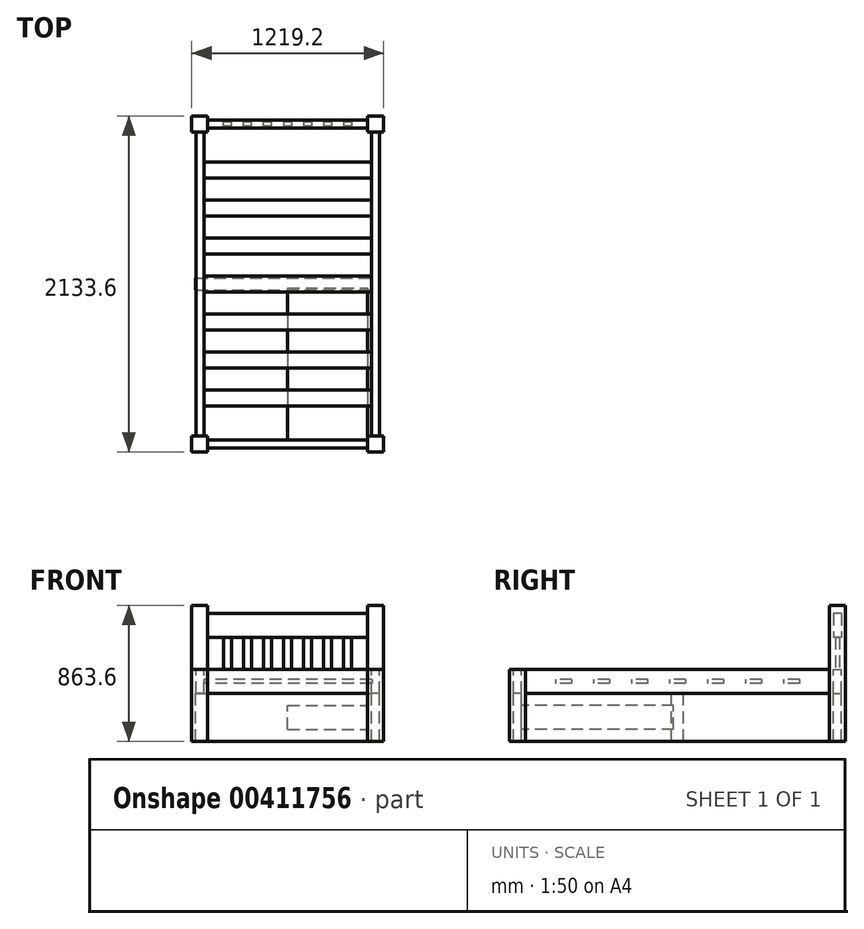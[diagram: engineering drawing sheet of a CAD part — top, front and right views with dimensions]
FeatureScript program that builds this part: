
annotation { "Feature Type Name" : "Feature", "Feature Type Description" : "" }
export const myFeature = defineFeature(function(context is Context, id is Id, definition is map)
    precondition{}
    {
        {
            var Q0;
            Q0=qCreatedBy(makeId("Top.planeOp"),FACE);
            var sketch = newSketch(context, id + "F0", { "sketchPlane" : qUnion([Q0])});
            skLineSegment(sketch, "E0.bottom", {"start": v(0, 0) * mm, "end": v(1219.2, 0) * mm});
            skLineSegment(sketch, "E0.top", {"start": v(0, 2133.6) * mm, "end": v(1219.2, 2133.6) * mm});
            skLineSegment(sketch, "E0.left", {"start": v(0, 0) * mm, "end": v(0, 2133.6) * mm});
            skLineSegment(sketch, "E0.right", {"start": v(1219.2, 0) * mm, "end": v(1219.2, 2133.6) * mm});
            skSolve(sketch);
        }
        {
            var Q0;
            Q0 = qSketchRegion(id + "F0", true);
            extrude(context, id + "F1", {"entities" : qUnion([Q0]), "depth" : 609.6 * mm});
        }
        {
            var Q0;
            Q0=makeQuery(id+"F1.opExtrude","CAP_FACE",FACE,{"disambiguationData":[OSD([sQuery(id+"F0.wireOp",EDGE,"E0.bottom"),sQuery(id+"F0.wireOp",EDGE,"E0.top"),sQuery(id+"F0.wireOp",EDGE,"E0.left"),sQuery(id+"F0.wireOp",EDGE,"E0.right")])],"isStart":false});
            var sketch = newSketch(context, id + "F2", { "sketchPlane" : qUnion([Q0])});
            skLineSegment(sketch, "E1.bottom", {"start": v(101.6, 0) * mm, "end": v(0, 0) * mm});
            skLineSegment(sketch, "E1.top", {"start": v(101.6, 101.6) * mm, "end": v(0, 101.6) * mm});
            skLineSegment(sketch, "E1.left", {"start": v(101.6, 0) * mm, "end": v(101.6, 101.6) * mm});
            skLineSegment(sketch, "E1.right", {"start": v(0, 0) * mm, "end": v(0, 101.6) * mm});
            skLineSegment(sketch, "E2.bottom", {"start": v(1117.6, 0) * mm, "end": v(1219.2, 0) * mm});
            skLineSegment(sketch, "E2.top", {"start": v(1117.6, 101.6) * mm, "end": v(1219.2, 101.6) * mm});
            skLineSegment(sketch, "E2.left", {"start": v(1117.6, 0) * mm, "end": v(1117.6, 101.6) * mm});
            skLineSegment(sketch, "E2.right", {"start": v(1219.2, 0) * mm, "end": v(1219.2, 101.6) * mm});
            skLineSegment(sketch, "E3.bottom", {"start": v(0, 2133.6) * mm, "end": v(101.6, 2133.6) * mm});
            skLineSegment(sketch, "E3.top", {"start": v(0, 2032) * mm, "end": v(101.6, 2032) * mm});
            skLineSegment(sketch, "E3.left", {"start": v(0, 2133.6) * mm, "end": v(0, 2032) * mm});
            skLineSegment(sketch, "E3.right", {"start": v(101.6, 2133.6) * mm, "end": v(101.6, 2032) * mm});
            skLineSegment(sketch, "E4.bottom", {"start": v(1219.2, 2133.6) * mm, "end": v(1117.6, 2133.6) * mm});
            skLineSegment(sketch, "E4.top", {"start": v(1219.2, 2032) * mm, "end": v(1117.6, 2032) * mm});
            skLineSegment(sketch, "E4.left", {"start": v(1219.2, 2133.6) * mm, "end": v(1219.2, 2032) * mm});
            skLineSegment(sketch, "E4.right", {"start": v(1117.6, 2133.6) * mm, "end": v(1117.6, 2032) * mm});
            skSolve(sketch);
        }
        {
            var Q0;
            {var subQ3=sQuery(id+"F2.wireOp",EDGE,"E1.top");Q0=makeQuery(id+"F2.imprint","IMPRINT",FACE,{"disambiguationData":[TD([[makeQuery(id+"F2.imprint","IMPRINT",EDGE,{"derivedFrom":subQ3}),-1.0]])]});}
            extrude(context, id + "F3", {"entities" : qUnion([Q0]), "operationType" : NewBodyOperationType.REMOVE, "oppositeDirection" : true, "depth" : 609.6 * mm});
        }
        {
            var Q0;
            Q0=makeQuery(id+"F3.boolean.opBoolean","COPY",FACE,{"derivedFrom":makeQuery(id+"F3.opExtrude","SWEPT_FACE",FACE,{"disambiguationData":[OSD([sQuery(id+"F2.wireOp",EDGE,"E3.top")])]})});
            var sketch = newSketch(context, id + "F4", { "sketchPlane" : qUnion([Q0])});
            skLineSegment(sketch, "E5", {"start": v(50.8, 0) * mm, "end": v(50.8, 609.6) * mm});
            skLineSegment(sketch, "E6", {"start": v(50.8, 0) * mm, "end": v(50.8, 304.8) * mm});
            skLineSegment(sketch, "E7.bottom", {"start": v(50.8, 304.8) * mm, "end": v(27.17, 304.8) * mm});
            skLineSegment(sketch, "E7.top", {"start": v(50.8, 457.2) * mm, "end": v(27.17, 457.2) * mm});
            skLineSegment(sketch, "E7.left", {"start": v(50.8, 304.8) * mm, "end": v(50.8, 457.2) * mm});
            skLineSegment(sketch, "E7.right", {"start": v(27.17, 304.8) * mm, "end": v(27.17, 457.2) * mm});
            skLineSegment(sketch, "E8.bottom", {"start": v(50.8, 304.8) * mm, "end": v(77.97, 304.8) * mm});
            skLineSegment(sketch, "E8.top", {"start": v(50.8, 457.2) * mm, "end": v(77.97, 457.2) * mm});
            skLineSegment(sketch, "E8.right", {"start": v(77.97, 304.8) * mm, "end": v(77.97, 457.2) * mm});
            skSolve(sketch);
        }
        {
            var Q0;
            Q0 = qSketchRegion(id + "F4", true);
            extrude(context, id + "F5", {"entities" : qUnion([Q0]), "depth" : 1930.4 * mm});
        }
        {
            var Q0;
            Q0=makeQuery(id+"F3.boolean.opBoolean","COPY",FACE,{"derivedFrom":makeQuery(id+"F3.opExtrude","SWEPT_FACE",FACE,{"disambiguationData":[OSD([sQuery(id+"F2.wireOp",EDGE,"E1.left")])]})});
            var sketch = newSketch(context, id + "F6", { "sketchPlane" : qUnion([Q0])});
            skLineSegment(sketch, "E9", {"start": v(50.8, 0) * mm, "end": v(50.8, 609.6) * mm});
            skLineSegment(sketch, "E10", {"start": v(50.8, 609.6) * mm, "end": v(50.8, 304.8) * mm});
            skLineSegment(sketch, "E11.bottom", {"start": v(50.8, 304.8) * mm, "end": v(25.4, 304.8) * mm});
            skLineSegment(sketch, "E11.top", {"start": v(50.8, 457.2) * mm, "end": v(25.4, 457.2) * mm});
            skLineSegment(sketch, "E11.left", {"start": v(50.8, 304.8) * mm, "end": v(50.8, 457.2) * mm});
            skLineSegment(sketch, "E11.right", {"start": v(25.4, 304.8) * mm, "end": v(25.4, 457.2) * mm});
            skLineSegment(sketch, "E12.bottom", {"start": v(50.8, 304.8) * mm, "end": v(76.2, 304.8) * mm});
            skLineSegment(sketch, "E12.top", {"start": v(50.8, 457.2) * mm, "end": v(76.2, 457.2) * mm});
            skLineSegment(sketch, "E12.right", {"start": v(76.2, 304.8) * mm, "end": v(76.2, 457.2) * mm});
            skSolve(sketch);
        }
        {
            var Q0;
            Q0=makeQuery(id+"F6.imprint","IMPRINT",FACE,{"disambiguationData":[TD([[makeQuery(id+"F6.imprint","IMPRINT",EDGE,{"derivedFrom":sQuery(id+"F6.wireOp",EDGE,"E11.bottom")}),-1.0]])]});
            var Q1;
            Q1=makeQuery(id+"F6.imprint","IMPRINT",FACE,{"disambiguationData":[TD([[makeQuery(id+"F6.imprint","IMPRINT",EDGE,{"derivedFrom":sQuery(id+"F6.wireOp",EDGE,"E12.bottom")}),1.0]])]});
            extrude(context, id + "F7", {"entities" : qUnion([Q0, Q1]), "depth" : 1016 * mm});
        }
        {
            var Q0;
            Q0=makeQuery(id+"F3.boolean.opBoolean","COPY",FACE,{"derivedFrom":makeQuery(id+"F3.opExtrude","SWEPT_FACE",FACE,{"disambiguationData":[OSD([sQuery(id+"F2.wireOp",EDGE,"E2.top")])]})});
            var sketch = newSketch(context, id + "F8", { "sketchPlane" : qUnion([Q0])});
            skLineSegment(sketch, "E13", {"start": v(-1168.4, 0) * mm, "end": v(-1168.4, 609.6) * mm});
            skLineSegment(sketch, "E14", {"start": v(-1168.4, 609.6) * mm, "end": v(-1168.4, 304.8) * mm});
            skLineSegment(sketch, "E15.bottom", {"start": v(-1168.4, 304.8) * mm, "end": v(-1193.8, 304.8) * mm});
            skLineSegment(sketch, "E15.top", {"start": v(-1168.4, 457.2) * mm, "end": v(-1193.8, 457.2) * mm});
            skLineSegment(sketch, "E15.left", {"start": v(-1168.4, 304.8) * mm, "end": v(-1168.4, 457.2) * mm});
            skLineSegment(sketch, "E15.right", {"start": v(-1193.8, 304.8) * mm, "end": v(-1193.8, 457.2) * mm});
            skLineSegment(sketch, "E16.bottom", {"start": v(-1168.4, 304.8) * mm, "end": v(-1143, 304.8) * mm});
            skLineSegment(sketch, "E16.top", {"start": v(-1168.4, 457.2) * mm, "end": v(-1143, 457.2) * mm});
            skLineSegment(sketch, "E16.right", {"start": v(-1143, 304.8) * mm, "end": v(-1143, 457.2) * mm});
            skSolve(sketch);
        }
        {
            var Q0;
            Q0=makeQuery(id+"F8.imprint","IMPRINT",FACE,{"disambiguationData":[TD([[makeQuery(id+"F8.imprint","IMPRINT",EDGE,{"derivedFrom":sQuery(id+"F8.wireOp",EDGE,"E16.bottom")}),1.0]])]});
            var Q1;
            Q1=makeQuery(id+"F8.imprint","IMPRINT",FACE,{"disambiguationData":[TD([[makeQuery(id+"F8.imprint","IMPRINT",EDGE,{"derivedFrom":sQuery(id+"F8.wireOp",EDGE,"E16.bottom")}),1.0]])]});
            var Q2;
            Q2=makeQuery(id+"F8.imprint","IMPRINT",FACE,{"disambiguationData":[TD([[makeQuery(id+"F8.imprint","IMPRINT",EDGE,{"derivedFrom":sQuery(id+"F8.wireOp",EDGE,"E15.bottom")}),-1.0]])]});
            extrude(context, id + "F9", {"entities" : qUnion([Q0, Q1, Q2]), "depth" : 1930.4 * mm});
        }
        {
            var Q0;
            Q0=makeQuery(id+"F3.boolean.opBoolean","COPY",FACE,{"derivedFrom":makeQuery(id+"F3.opExtrude","SWEPT_FACE",FACE,{"disambiguationData":[OSD([sQuery(id+"F2.wireOp",EDGE,"E4.right")])]})});
            var sketch = newSketch(context, id + "F10", { "sketchPlane" : qUnion([Q0])});
            skLineSegment(sketch, "E17", {"start": v(-2082.8, 0) * mm, "end": v(-2082.8, 609.6) * mm});
            skLineSegment(sketch, "E18", {"start": v(-2082.8, 0) * mm, "end": v(-2082.8, 304.8) * mm});
            skLineSegment(sketch, "E19.bottom", {"start": v(-2082.8, 304.8) * mm, "end": v(-2108.2, 304.8) * mm});
            skLineSegment(sketch, "E19.top", {"start": v(-2082.8, 457.2) * mm, "end": v(-2108.2, 457.2) * mm});
            skLineSegment(sketch, "E19.left", {"start": v(-2082.8, 304.8) * mm, "end": v(-2082.8, 457.2) * mm});
            skLineSegment(sketch, "E19.right", {"start": v(-2108.2, 304.8) * mm, "end": v(-2108.2, 457.2) * mm});
            skLineSegment(sketch, "E20.bottom", {"start": v(-2082.8, 304.8) * mm, "end": v(-2057.4, 304.8) * mm});
            skLineSegment(sketch, "E20.top", {"start": v(-2082.8, 457.2) * mm, "end": v(-2057.4, 457.2) * mm});
            skLineSegment(sketch, "E20.right", {"start": v(-2057.4, 304.8) * mm, "end": v(-2057.4, 457.2) * mm});
            skSolve(sketch);
        }
        {
            var Q0;
            Q0 = qSketchRegion(id + "F10", true);
            extrude(context, id + "F11", {"entities" : qUnion([Q0]), "depth" : 1016 * mm});
        }
        {
            var Q0;
            {var subQ0=sQuery(id+"F0.wireOp",EDGE,"E0.bottom");var subQ1=sQuery(id+"F0.wireOp",EDGE,"E0.left");Q0=makeQuery(id+"F3.boolean.opBoolean","SPLIT",FACE,{"disambiguationData":[TD([makeQuery(id+"F3.opExtrude","SWEPT_FACE",FACE,{"disambiguationData":[OSD([sQuery(id+"F2.wireOp",EDGE,"E1.top")])]})])],"derivedFrom":makeQuery(id+"F1.opExtrude","CAP_FACE",FACE,{"disambiguationData":[OSD([subQ0,sQuery(id+"F0.wireOp",EDGE,"E0.top"),subQ1,sQuery(id+"F0.wireOp",EDGE,"E0.right")])],"isStart":false})});}
            var sketch = newSketch(context, id + "F12", { "sketchPlane" : qUnion([Q0])});
            skSolve(sketch);
        }
        {
            var Q0;
            Q0=makeQuery(id+"F5.opExtrude","SWEPT_FACE",FACE,{"disambiguationData":[OSD([sQuery(id+"F4.wireOp",EDGE,"E8.right")])]});
            var sketch = newSketch(context, id + "F13", { "sketchPlane" : qUnion([Q0])});
            skLineSegment(sketch, "E21", {"start": v(101.6, 381) * mm, "end": v(342.9, 381) * mm});
            skPoint(sketch, "E21.endSnap0", {"position": v(101.6, 381) * mm});
            skLineSegment(sketch, "E22", {"start": v(1066.8, 381) * mm, "end": v(342.9, 381) * mm});
            skLineSegment(sketch, "E23", {"start": v(1790.7, 381) * mm, "end": v(1066.8, 381) * mm});
            skLineSegment(sketch, "E24", {"start": v(2032, 381) * mm, "end": v(1790.7, 381) * mm});
            skLineSegment(sketch, "E25", {"start": v(342.9, 381) * mm, "end": v(584.2, 381) * mm});
            skLineSegment(sketch, "E26", {"start": v(825.5, 381) * mm, "end": v(584.2, 381) * mm});
            skLineSegment(sketch, "E27", {"start": v(1549.4, 381) * mm, "end": v(1790.7, 381) * mm});
            skLineSegment(sketch, "E28", {"start": v(1308.1, 381) * mm, "end": v(1549.4, 381) * mm});
            skLineSegment(sketch, "E29.bottom", {"start": v(393.7, 393.7) * mm, "end": v(292.1, 393.7) * mm});
            skLineSegment(sketch, "E29.top", {"start": v(393.7, 368.3) * mm, "end": v(292.1, 368.3) * mm});
            skLineSegment(sketch, "E29.left", {"start": v(393.7, 393.7) * mm, "end": v(393.7, 368.3) * mm});
            skLineSegment(sketch, "E29.right", {"start": v(292.1, 393.7) * mm, "end": v(292.1, 368.3) * mm});
            skPoint(sketch, "E29.middle", {"position": v(342.9, 381) * mm});
            skLineSegment(sketch, "E30.bottom", {"start": v(292.1, 393.7) * mm, "end": v(393.7, 393.7) * mm});
            skLineSegment(sketch, "E30.top", {"start": v(292.1, 393.7) * mm, "end": v(393.7, 393.7) * mm});
            skLineSegment(sketch, "E30.left", {"start": v(292.1, 393.7) * mm, "end": v(292.1, 393.7) * mm});
            skLineSegment(sketch, "E30.right", {"start": v(393.7, 393.7) * mm, "end": v(393.7, 393.7) * mm});
            skPoint(sketch, "E30.middle", {"position": v(342.9, 393.7) * mm});
            skLineSegment(sketch, "E31.bottom", {"start": v(635, 393.7) * mm, "end": v(533.4, 393.7) * mm});
            skLineSegment(sketch, "E31.top", {"start": v(635, 368.3) * mm, "end": v(533.4, 368.3) * mm});
            skLineSegment(sketch, "E31.left", {"start": v(635, 393.7) * mm, "end": v(635, 368.3) * mm});
            skLineSegment(sketch, "E31.right", {"start": v(533.4, 393.7) * mm, "end": v(533.4, 368.3) * mm});
            skPoint(sketch, "E31.middle", {"position": v(584.2, 381) * mm});
            skLineSegment(sketch, "E32.bottom", {"start": v(876.3, 393.7) * mm, "end": v(774.7, 393.7) * mm});
            skLineSegment(sketch, "E32.top", {"start": v(876.3, 368.3) * mm, "end": v(774.7, 368.3) * mm});
            skLineSegment(sketch, "E32.left", {"start": v(876.3, 393.7) * mm, "end": v(876.3, 368.3) * mm});
            skLineSegment(sketch, "E32.right", {"start": v(774.7, 393.7) * mm, "end": v(774.7, 368.3) * mm});
            skPoint(sketch, "E32.middle", {"position": v(825.5, 381) * mm});
            skLineSegment(sketch, "E33.bottom", {"start": v(1117.6, 393.7) * mm, "end": v(1016, 393.7) * mm});
            skLineSegment(sketch, "E33.top", {"start": v(1117.6, 368.3) * mm, "end": v(1016, 368.3) * mm});
            skLineSegment(sketch, "E33.left", {"start": v(1117.6, 393.7) * mm, "end": v(1117.6, 368.3) * mm});
            skLineSegment(sketch, "E33.right", {"start": v(1016, 393.7) * mm, "end": v(1016, 368.3) * mm});
            skPoint(sketch, "E33.middle", {"position": v(1066.8, 381) * mm});
            skLineSegment(sketch, "E34.bottom", {"start": v(1358.9, 393.7) * mm, "end": v(1257.3, 393.7) * mm});
            skLineSegment(sketch, "E34.top", {"start": v(1358.9, 368.3) * mm, "end": v(1257.3, 368.3) * mm});
            skLineSegment(sketch, "E34.left", {"start": v(1358.9, 393.7) * mm, "end": v(1358.9, 368.3) * mm});
            skLineSegment(sketch, "E34.right", {"start": v(1257.3, 393.7) * mm, "end": v(1257.3, 368.3) * mm});
            skPoint(sketch, "E34.middle", {"position": v(1308.1, 381) * mm});
            skLineSegment(sketch, "E35.bottom", {"start": v(1600.2, 393.7) * mm, "end": v(1498.6, 393.7) * mm});
            skLineSegment(sketch, "E35.top", {"start": v(1600.2, 368.3) * mm, "end": v(1498.6, 368.3) * mm});
            skLineSegment(sketch, "E35.left", {"start": v(1600.2, 393.7) * mm, "end": v(1600.2, 368.3) * mm});
            skLineSegment(sketch, "E35.right", {"start": v(1498.6, 393.7) * mm, "end": v(1498.6, 368.3) * mm});
            skPoint(sketch, "E35.middle", {"position": v(1549.4, 381) * mm});
            skLineSegment(sketch, "E36.bottom", {"start": v(1841.5, 393.7) * mm, "end": v(1739.9, 393.7) * mm});
            skLineSegment(sketch, "E36.top", {"start": v(1841.5, 368.3) * mm, "end": v(1739.9, 368.3) * mm});
            skLineSegment(sketch, "E36.left", {"start": v(1841.5, 393.7) * mm, "end": v(1841.5, 368.3) * mm});
            skLineSegment(sketch, "E36.right", {"start": v(1739.9, 393.7) * mm, "end": v(1739.9, 368.3) * mm});
            skPoint(sketch, "E36.middle", {"position": v(1790.7, 381) * mm});
            skSolve(sketch);
        }
        {
            var Q0;
            Q0 = qSketchRegion(id + "F13", true);
            extrude(context, id + "F14", {"entities" : qUnion([Q0]), "depth" : 1066.8 * mm});
        }
        {
            var Q0;
            {var subQ0=sQuery(id+"F0.wireOp",EDGE,"E0.top");var subQ1=sQuery(id+"F0.wireOp",EDGE,"E0.right");Q0=makeQuery(id+"F3.boolean.opBoolean","SPLIT",FACE,{"disambiguationData":[TD([makeQuery(id+"F3.opExtrude","SWEPT_FACE",FACE,{"disambiguationData":[OSD([sQuery(id+"F2.wireOp",EDGE,"E4.top")])]})])],"derivedFrom":makeQuery(id+"F1.opExtrude","CAP_FACE",FACE,{"disambiguationData":[OSD([sQuery(id+"F0.wireOp",EDGE,"E0.bottom"),subQ0,sQuery(id+"F0.wireOp",EDGE,"E0.left"),subQ1])],"isStart":false})});}
            var sketch = newSketch(context, id + "F15", { "sketchPlane" : qUnion([Q0])});
            skLineSegment(sketch, "E37.bottom", {"start": v(1117.6, 2032) * mm, "end": v(1219.2, 2032) * mm});
            skLineSegment(sketch, "E37.top", {"start": v(1117.6, 2133.6) * mm, "end": v(1219.2, 2133.6) * mm});
            skLineSegment(sketch, "E37.left", {"start": v(1117.6, 2032) * mm, "end": v(1117.6, 2133.6) * mm});
            skLineSegment(sketch, "E37.right", {"start": v(1219.2, 2032) * mm, "end": v(1219.2, 2133.6) * mm});
            skSolve(sketch);
        }
        {
            var Q0;
            Q0 = qSketchRegion(id + "F15", true);
            extrude(context, id + "F16", {"entities" : qUnion([Q0]), "operationType" : NewBodyOperationType.ADD, "depth" : 254 * mm});
        }
        {
            var Q0;
            {var subQ0=sQuery(id+"F0.wireOp",EDGE,"E0.top");var subQ1=sQuery(id+"F0.wireOp",EDGE,"E0.left");Q0=makeQuery(id+"F3.boolean.opBoolean","SPLIT",FACE,{"disambiguationData":[TD([makeQuery(id+"F3.opExtrude","SWEPT_FACE",FACE,{"disambiguationData":[OSD([sQuery(id+"F2.wireOp",EDGE,"E3.top")])]})])],"derivedFrom":makeQuery(id+"F1.opExtrude","CAP_FACE",FACE,{"disambiguationData":[OSD([sQuery(id+"F0.wireOp",EDGE,"E0.bottom"),subQ0,subQ1,sQuery(id+"F0.wireOp",EDGE,"E0.right")])],"isStart":false})});}
            var sketch = newSketch(context, id + "F17", { "sketchPlane" : qUnion([Q0])});
            skLineSegment(sketch, "E38.bottom", {"start": v(0, 2032) * mm, "end": v(101.6, 2032) * mm});
            skLineSegment(sketch, "E38.top", {"start": v(0, 2133.6) * mm, "end": v(101.6, 2133.6) * mm});
            skLineSegment(sketch, "E38.left", {"start": v(0, 2032) * mm, "end": v(0, 2133.6) * mm});
            skLineSegment(sketch, "E38.right", {"start": v(101.6, 2032) * mm, "end": v(101.6, 2133.6) * mm});
            skSolve(sketch);
        }
        {
            var Q0;
            Q0 = qSketchRegion(id + "F17", true);
            extrude(context, id + "F18", {"entities" : qUnion([Q0]), "operationType" : NewBodyOperationType.ADD, "depth" : 254 * mm});
        }
        {
            var Q0;
            Q0=makeQuery(id+"F18.boolean.opBoolean","MERGE",FACE,{"derivedFrom":[makeQuery(id+"F3.boolean.opBoolean","COPY",FACE,{"derivedFrom":makeQuery(id+"F3.opExtrude","SWEPT_FACE",FACE,{"disambiguationData":[OSD([sQuery(id+"F2.wireOp",EDGE,"E3.right")])]})}),makeQuery(id+"F18.opExtrude","SWEPT_FACE",FACE,{"disambiguationData":[OSD([sQuery(id+"F17.wireOp",EDGE,"E38.right")])]})]});
            var sketch = newSketch(context, id + "F19", { "sketchPlane" : qUnion([Q0])});
            skLineSegment(sketch, "E39", {"start": v(2082.8, 863.6) * mm, "end": v(2082.8, 473.13) * mm});
            skPoint(sketch, "E39.endSnap0", {"position": v(2082.8, 863.6) * mm});
            skLineSegment(sketch, "E40", {"start": v(2082.8, 473.13) * mm, "end": v(2082.8, 456.9) * mm});
            skLineSegment(sketch, "E41", {"start": v(2082.8, 456.9) * mm, "end": v(2082.8, 812.8) * mm});
            skLineSegment(sketch, "E42.bottom", {"start": v(2108.2, 812.8) * mm, "end": v(2057.4, 812.8) * mm});
            skLineSegment(sketch, "E42.top", {"start": v(2108.2, 660.4) * mm, "end": v(2057.4, 660.4) * mm});
            skLineSegment(sketch, "E42.left", {"start": v(2108.2, 812.8) * mm, "end": v(2108.2, 660.4) * mm});
            skLineSegment(sketch, "E42.right", {"start": v(2057.4, 812.8) * mm, "end": v(2057.4, 660.4) * mm});
            skPoint(sketch, "E42.middle", {"position": v(2082.8, 736.6) * mm});
            skSolve(sketch);
        }
        {
            var Q0;
            Q0 = qSketchRegion(id + "F19", true);
            extrude(context, id + "F20", {"entities" : qUnion([Q0]), "depth" : 1016 * mm});
        }
        {
            var Q0;
            Q0=makeQuery(id+"F11.opExtrude","SWEPT_FACE",FACE,{"disambiguationData":[OSD([sQuery(id+"F10.wireOp",EDGE,"E19.top"),sQuery(id+"F10.wireOp",EDGE,"E20.top")])]});
            var sketch = newSketch(context, id + "F21", { "sketchPlane" : qUnion([Q0])});
            skLineSegment(sketch, "E43", {"start": v(101.6, 2082.8) * mm, "end": v(609.6, 2082.8) * mm});
            skLineSegment(sketch, "E44", {"start": v(609.6, 2082.8) * mm, "end": v(863.6, 2082.8) * mm});
            skLineSegment(sketch, "E45", {"start": v(863.6, 2082.8) * mm, "end": v(1117.6, 2082.8) * mm});
            skLineSegment(sketch, "E46", {"start": v(990.6, 2082.8) * mm, "end": v(1117.6, 2082.8) * mm});
            skLineSegment(sketch, "E47", {"start": v(736.6, 2082.8) * mm, "end": v(609.6, 2082.8) * mm});
            skLineSegment(sketch, "E48", {"start": v(609.6, 2082.8) * mm, "end": v(355.6, 2082.8) * mm});
            skLineSegment(sketch, "E49", {"start": v(355.6, 2082.8) * mm, "end": v(227.11, 2082.8) * mm});
            skLineSegment(sketch, "E50", {"start": v(227.11, 2082.8) * mm, "end": v(482.6, 2082.8) * mm});
            skLineSegment(sketch, "E51.bottom", {"start": v(252.51, 2070.1) * mm, "end": v(201.71, 2070.1) * mm});
            skLineSegment(sketch, "E51.top", {"start": v(252.51, 2095.5) * mm, "end": v(201.71, 2095.5) * mm});
            skLineSegment(sketch, "E51.left", {"start": v(252.51, 2070.1) * mm, "end": v(252.51, 2095.5) * mm});
            skLineSegment(sketch, "E51.right", {"start": v(201.71, 2070.1) * mm, "end": v(201.71, 2095.5) * mm});
            skPoint(sketch, "E51.middle", {"position": v(227.11, 2082.8) * mm});
            skLineSegment(sketch, "E52.bottom", {"start": v(381, 2070.1) * mm, "end": v(330.2, 2070.1) * mm});
            skLineSegment(sketch, "E52.top", {"start": v(381, 2095.5) * mm, "end": v(330.2, 2095.5) * mm});
            skLineSegment(sketch, "E52.left", {"start": v(381, 2070.1) * mm, "end": v(381, 2095.5) * mm});
            skLineSegment(sketch, "E52.right", {"start": v(330.2, 2070.1) * mm, "end": v(330.2, 2095.5) * mm});
            skPoint(sketch, "E52.middle", {"position": v(355.6, 2082.8) * mm});
            skLineSegment(sketch, "E53.bottom", {"start": v(508, 2070.1) * mm, "end": v(457.2, 2070.1) * mm});
            skLineSegment(sketch, "E53.top", {"start": v(508, 2095.5) * mm, "end": v(457.2, 2095.5) * mm});
            skLineSegment(sketch, "E53.left", {"start": v(508, 2070.1) * mm, "end": v(508, 2095.5) * mm});
            skLineSegment(sketch, "E53.right", {"start": v(457.2, 2070.1) * mm, "end": v(457.2, 2095.5) * mm});
            skPoint(sketch, "E53.middle", {"position": v(482.6, 2082.8) * mm});
            skLineSegment(sketch, "E54.bottom", {"start": v(635, 2095.5) * mm, "end": v(584.2, 2095.5) * mm});
            skLineSegment(sketch, "E54.top", {"start": v(635, 2070.1) * mm, "end": v(584.2, 2070.1) * mm});
            skLineSegment(sketch, "E54.left", {"start": v(635, 2095.5) * mm, "end": v(635, 2070.1) * mm});
            skLineSegment(sketch, "E54.right", {"start": v(584.2, 2095.5) * mm, "end": v(584.2, 2070.1) * mm});
            skPoint(sketch, "E54.middle", {"position": v(609.6, 2082.8) * mm});
            skLineSegment(sketch, "E55.bottom", {"start": v(762, 2095.5) * mm, "end": v(711.2, 2095.5) * mm});
            skLineSegment(sketch, "E55.top", {"start": v(762, 2070.1) * mm, "end": v(711.2, 2070.1) * mm});
            skLineSegment(sketch, "E55.left", {"start": v(762, 2095.5) * mm, "end": v(762, 2070.1) * mm});
            skLineSegment(sketch, "E55.right", {"start": v(711.2, 2095.5) * mm, "end": v(711.2, 2070.1) * mm});
            skPoint(sketch, "E55.middle", {"position": v(736.6, 2082.8) * mm});
            skLineSegment(sketch, "E56.bottom", {"start": v(889, 2095.5) * mm, "end": v(838.2, 2095.5) * mm});
            skLineSegment(sketch, "E56.top", {"start": v(889, 2070.1) * mm, "end": v(838.2, 2070.1) * mm});
            skLineSegment(sketch, "E56.left", {"start": v(889, 2095.5) * mm, "end": v(889, 2070.1) * mm});
            skLineSegment(sketch, "E56.right", {"start": v(838.2, 2095.5) * mm, "end": v(838.2, 2070.1) * mm});
            skPoint(sketch, "E56.middle", {"position": v(863.6, 2082.8) * mm});
            skLineSegment(sketch, "E57.bottom", {"start": v(1016, 2095.5) * mm, "end": v(965.2, 2095.5) * mm});
            skLineSegment(sketch, "E57.top", {"start": v(1016, 2070.1) * mm, "end": v(965.2, 2070.1) * mm});
            skLineSegment(sketch, "E57.left", {"start": v(1016, 2095.5) * mm, "end": v(1016, 2070.1) * mm});
            skLineSegment(sketch, "E57.right", {"start": v(965.2, 2095.5) * mm, "end": v(965.2, 2070.1) * mm});
            skPoint(sketch, "E57.middle", {"position": v(990.6, 2082.8) * mm});
            skSolve(sketch);
        }
        {
            var Q0;
            Q0 = qSketchRegion(id + "F21", true);
            extrude(context, id + "F22", {"entities" : qUnion([Q0]), "depth" : 203.2 * mm});
        }
        {
            var Q0;
            {var subQ0=sQuery(id+"F0.wireOp",EDGE,"E0.bottom");var subQ1=sQuery(id+"F0.wireOp",EDGE,"E0.right");Q0=makeQuery(id+"F3.boolean.opBoolean","SPLIT",FACE,{"disambiguationData":[TD([makeQuery(id+"F3.opExtrude","SWEPT_FACE",FACE,{"disambiguationData":[OSD([sQuery(id+"F2.wireOp",EDGE,"E2.top")])]})])],"derivedFrom":makeQuery(id+"F1.opExtrude","CAP_FACE",FACE,{"disambiguationData":[OSD([subQ0,sQuery(id+"F0.wireOp",EDGE,"E0.top"),sQuery(id+"F0.wireOp",EDGE,"E0.left"),subQ1])],"isStart":false})});}
            var sketch = newSketch(context, id + "F23", { "sketchPlane" : qUnion([Q0])});
            skLineSegment(sketch, "E58.bottom", {"start": v(1117.6, 0) * mm, "end": v(1219.2, 0) * mm});
            skLineSegment(sketch, "E58.top", {"start": v(1117.6, 101.6) * mm, "end": v(1219.2, 101.6) * mm});
            skLineSegment(sketch, "E58.left", {"start": v(1117.6, 0) * mm, "end": v(1117.6, 101.6) * mm});
            skLineSegment(sketch, "E58.right", {"start": v(1219.2, 0) * mm, "end": v(1219.2, 101.6) * mm});
            skSolve(sketch);
        }
        {
            var Q0;
            Q0 = qSketchRegion(id + "F23", true);
            extrude(context, id + "F24", {"entities" : qUnion([Q0]), "operationType" : NewBodyOperationType.REMOVE, "oppositeDirection" : true, "depth" : 76.2 * mm});
        }
        {
            var Q0;
            Q0=makeQuery(id+"F24.boolean.opBoolean","COPY",FACE,{"derivedFrom":makeQuery(id+"F24.opExtrude","CAP_FACE",FACE,{"disambiguationData":[OSD([sQuery(id+"F23.wireOp",EDGE,"E58.bottom"),sQuery(id+"F23.wireOp",EDGE,"E58.top"),sQuery(id+"F23.wireOp",EDGE,"E58.left"),sQuery(id+"F23.wireOp",EDGE,"E58.right")])],"isStart":false})});
            extrude(context, id + "F25", {"entities" : qUnion([Q0]), "operationType" : NewBodyOperationType.REMOVE, "oppositeDirection" : true, "depth" : 76.2 * mm});
        }
        {
            var Q0;
            {var subQ0=sQuery(id+"F2.wireOp",EDGE,"E1.top");Q0=makeQuery(id+"F12.imprint","IMPRINT",FACE,{"disambiguationData":[TD([[makeQuery(id+"F12.imprint","IMPRINT",EDGE,{"derivedFrom":makeQuery(id+"F3.boolean.opBoolean","COPY",EDGE,{"derivedFrom":makeQuery(id+"F3.opExtrude","CAP_EDGE",EDGE,{"disambiguationData":[OSD([subQ0])],"isStart":true})})}),1.0]])]});}
            var sketch = newSketch(context, id + "F26", { "sketchPlane" : qUnion([Q0])});
            skLineSegment(sketch, "E59.bottom", {"start": v(101.43, 101.85) * mm, "end": v(0, 101.85) * mm});
            skLineSegment(sketch, "E59.top", {"start": v(101.43, 0) * mm, "end": v(0, 0) * mm});
            skLineSegment(sketch, "E59.left", {"start": v(101.43, 101.85) * mm, "end": v(101.43, 0) * mm});
            skLineSegment(sketch, "E59.right", {"start": v(0, 101.85) * mm, "end": v(0, 0) * mm});
            skSolve(sketch);
        }
        {
            var Q0;
            {var subQ0=sQuery(id+"F2.wireOp",EDGE,"E1.top");Q0=makeQuery(id+"F12.imprint","IMPRINT",FACE,{"disambiguationData":[TD([[makeQuery(id+"F12.imprint","IMPRINT",EDGE,{"derivedFrom":makeQuery(id+"F3.boolean.opBoolean","COPY",EDGE,{"derivedFrom":makeQuery(id+"F3.opExtrude","CAP_EDGE",EDGE,{"disambiguationData":[OSD([subQ0])],"isStart":true})})}),1.0]])]});}
            var Q1;
            {var subQ0=sQuery(id+"F26.wireOp",EDGE,"E59.bottom");Q1=makeQuery(id+"F26.imprint","IMPRINT",FACE,{"disambiguationData":[TD([[makeQuery(id+"F26.imprint","IMPRINT",EDGE,{"derivedFrom":subQ0}),1.0]])]});}
            extrude(context, id + "F27", {"entities" : qUnion([Q0, Q1]), "operationType" : NewBodyOperationType.REMOVE, "oppositeDirection" : true, "depth" : 152.4 * mm});
        }
        {
            var Q0;
            Q0=makeQuery(id+"F11.opExtrude","SWEPT_FACE",FACE,{"disambiguationData":[OSD([sQuery(id+"F10.wireOp",EDGE,"E19.bottom"),sQuery(id+"F10.wireOp",EDGE,"E20.bottom")])]});
            var sketch = newSketch(context, id + "F28", { "sketchPlane" : qUnion([Q0])});
            skSolve(sketch);
        }
        {
            var Q0;
            {var subQ0=sQuery(id+"F10.wireOp",EDGE,"E19.bottom");Q0=makeQuery(id+"F28.imprint","IMPRINT",FACE,{"disambiguationData":[TD([[makeQuery(id+"F28.imprint","IMPRINT",EDGE,{"derivedFrom":makeQuery(id+"F11.opExtrude","SWEPT_EDGE",EDGE,{"disambiguationData":[OSD([subQ0,sQuery(id+"F10.wireOp",EDGE,"E19.right")])]})}),1.0]])]});}
            extrude(context, id + "F29", {"entities" : qUnion([Q0]), "depth" : 304.8 * mm});
        }
        {
            var Q0;
            Q0=makeQuery(id+"F7.opExtrude","SWEPT_FACE",FACE,{"disambiguationData":[OSD([sQuery(id+"F6.wireOp",EDGE,"E11.bottom"),sQuery(id+"F6.wireOp",EDGE,"E12.bottom")])]});
            extrude(context, id + "F30", {"entities" : qUnion([Q0]), "depth" : 304.8 * mm});
        }
        {
            var Q0;
            Q0=makeQuery(id+"F9.opExtrude","SWEPT_FACE",FACE,{"disambiguationData":[OSD([sQuery(id+"F8.wireOp",EDGE,"E15.bottom"),sQuery(id+"F8.wireOp",EDGE,"E16.bottom")])]});
            var sketch = newSketch(context, id + "F31", { "sketchPlane" : qUnion([Q0])});
            skSolve(sketch);
        }
        {
            var Q0;
            {var subQ0=sQuery(id+"F8.wireOp",EDGE,"E15.bottom");Q0=makeQuery(id+"F31.imprint","IMPRINT",FACE,{"disambiguationData":[TD([[makeQuery(id+"F31.imprint","IMPRINT",EDGE,{"derivedFrom":makeQuery(id+"F9.opExtrude","SWEPT_EDGE",EDGE,{"disambiguationData":[OSD([subQ0,sQuery(id+"F8.wireOp",EDGE,"E15.right")])]})}),1.0]])]});}
            extrude(context, id + "F32", {"entities" : qUnion([Q0]), "depth" : 304.8 * mm});
        }
        {
            var Q0;
            Q0=makeQuery(id+"F30.opExtrude","SWEPT_FACE",FACE,{"disambiguationData":[OSD([sQuery(id+"F6.wireOp",EDGE,"E12.bottom"),sQuery(id+"F6.wireOp",EDGE,"E12.right")])]});
            var sketch = newSketch(context, id + "F33", { "sketchPlane" : qUnion([Q0])});
            skLineSegment(sketch, "E60", {"start": v(-1117.6, 76.2) * mm, "end": v(-1117.6, 0) * mm});
            skLineSegment(sketch, "E61", {"start": v(-609.6, 0) * mm, "end": v(-609.6, 76.2) * mm});
            skLineSegment(sketch, "E62", {"start": v(-609.6, 76.2) * mm, "end": v(-1117.6, 76.2) * mm});
            skLineSegment(sketch, "E63.bottom", {"start": v(-1117.6, 76.2) * mm, "end": v(-1117.6, 76.2) * mm});
            skLineSegment(sketch, "E63.top", {"start": v(-1117.6, 228.6) * mm, "end": v(-1117.6, 228.6) * mm});
            skLineSegment(sketch, "E63.left", {"start": v(-1117.6, 76.2) * mm, "end": v(-1117.6, 228.6) * mm});
            skLineSegment(sketch, "E63.right", {"start": v(-1117.6, 76.2) * mm, "end": v(-1117.6, 228.6) * mm});
            skLineSegment(sketch, "E64.top", {"start": v(-609.6, 228.6) * mm, "end": v(-1117.6, 228.6) * mm});
            skLineSegment(sketch, "E64.left", {"start": v(-609.6, 76.2) * mm, "end": v(-609.6, 228.6) * mm});
            skSolve(sketch);
        }
        {
            var Q0;
            Q0=makeQuery(id+"F32.opExtrude","CAP_FACE",FACE,{"disambiguationData":[OSD([sQuery(id+"F8.wireOp",EDGE,"E15.bottom"),sQuery(id+"F8.wireOp",EDGE,"E15.right"),sQuery(id+"F8.wireOp",EDGE,"E16.bottom"),sQuery(id+"F8.wireOp",EDGE,"E16.right")])],"isStart":false});
            var sketch = newSketch(context, id + "F34", { "sketchPlane" : qUnion([Q0])});
            skLineSegment(sketch, "E65", {"start": v(1193.8, -1066.8) * mm, "end": v(1143, -1066.8) * mm});
            skLineSegment(sketch, "E66", {"start": v(1143, -1066.8) * mm, "end": v(1143, -1104.9) * mm});
            skLineSegment(sketch, "E67", {"start": v(1143, -1066.8) * mm, "end": v(1143, -1028.7) * mm});
            skLineSegment(sketch, "E68.bottom", {"start": v(1143, -1028.7) * mm, "end": v(1193.8, -1028.7) * mm});
            skLineSegment(sketch, "E68.top", {"start": v(1143, -1104.9) * mm, "end": v(1193.8, -1104.9) * mm});
            skLineSegment(sketch, "E68.left", {"start": v(1143, -1028.7) * mm, "end": v(1143, -1104.9) * mm});
            skLineSegment(sketch, "E68.right", {"start": v(1193.8, -1028.7) * mm, "end": v(1193.8, -1104.9) * mm});
            skSolve(sketch);
        }
        {
            var Q0;
            Q0=makeQuery(id+"F32.opExtrude","SWEPT_FACE",FACE,{"disambiguationData":[OSD([sQuery(id+"F8.wireOp",EDGE,"E16.bottom"),sQuery(id+"F8.wireOp",EDGE,"E16.right")])]});
            var sketch = newSketch(context, id + "F35", { "sketchPlane" : qUnion([Q0])});
            skLineSegment(sketch, "E69", {"start": v(-1028.57, 0) * mm, "end": v(-1028.57, 304.8) * mm});
            skLineSegment(sketch, "E70", {"start": v(-1104.9, 0) * mm, "end": v(-1104.9, 304.8) * mm});
            skSolve(sketch);
        }
        {
            var Q0;
            {var subQ0=sQuery(id+"F35.wireOp",EDGE,"E69");Q0=makeQuery(id+"F35.imprint","IMPRINT",FACE,{"disambiguationData":[TD([[makeQuery(id+"F35.imprint","IMPRINT",EDGE,{"derivedFrom":subQ0}),1.0]])]});}
            extrude(context, id + "F36", {"entities" : qUnion([Q0]), "depth" : 1117.6 * mm});
        }
        {
            var Q0;
            Q0=makeQuery(id+"F33.imprint","IMPRINT",FACE,{"disambiguationData":[TD([[makeQuery(id+"F33.imprint","IMPRINT",EDGE,{"derivedFrom":sQuery(id+"F33.wireOp",EDGE,"E62")}),-1.0]])]});
            extrude(context, id + "F37", {"entities" : qUnion([Q0]), "depth" : 965.2 * mm});
        }
    });
